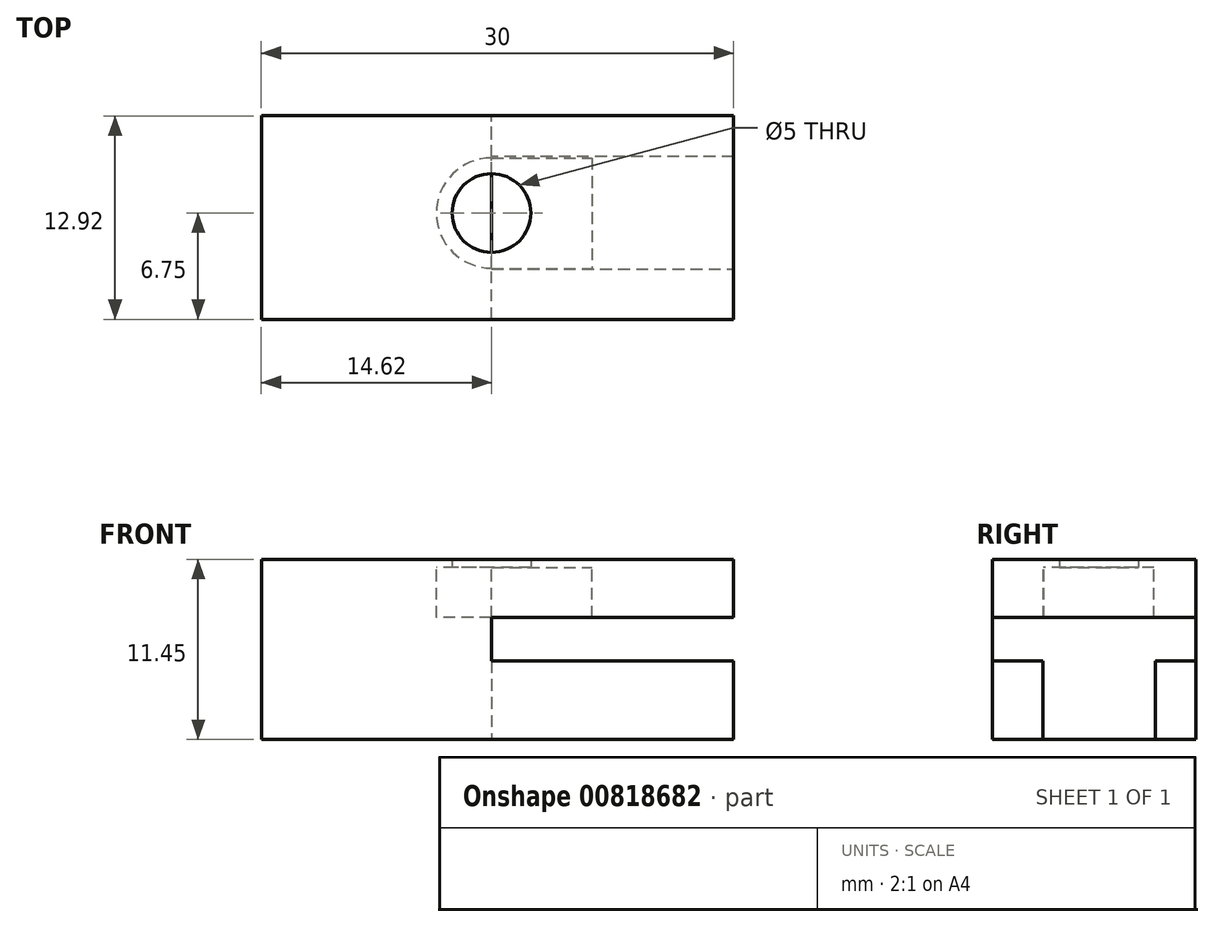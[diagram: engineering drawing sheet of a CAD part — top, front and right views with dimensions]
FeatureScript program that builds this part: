
annotation { "Feature Type Name" : "Feature", "Feature Type Description" : "" }
export const myFeature = defineFeature(function(context is Context, id is Id, definition is map)
    precondition{}
    {
        {
            var Q0;
            Q0=qCreatedBy(makeId("Top.planeOp"),FACE);
            var sketch = newSketch(context, id + "F0", { "sketchPlane" : qUnion([Q0])});
            skCircle(sketch, "E0", {"center": v(0, 0) * mm, "radius": 2.5 * mm});
            skCircle(sketch, "E1", {"center": v(0, 0) * mm, "radius": 3.5 * mm});
            skLineSegment(sketch, "E2.bottom", {"start": v(-14.62, 6.17) * mm, "end": v(15.38, 6.17) * mm});
            skLineSegment(sketch, "E2.top", {"start": v(-14.62, -6.75) * mm, "end": v(15.38, -6.75) * mm});
            skLineSegment(sketch, "E2.left", {"start": v(-14.62, 6.17) * mm, "end": v(-14.62, -6.75) * mm});
            skLineSegment(sketch, "E2.right", {"start": v(15.38, 6.17) * mm, "end": v(15.38, -6.75) * mm});
            skLineSegment(sketch, "E3.bottom", {"start": v(0, 3.5) * mm, "end": v(6.4, 3.5) * mm});
            skLineSegment(sketch, "E3.top", {"start": v(0, -3.52) * mm, "end": v(6.4, -3.52) * mm});
            skLineSegment(sketch, "E3.left", {"start": v(0, 3.5) * mm, "end": v(0, -3.52) * mm});
            skLineSegment(sketch, "E3.right", {"start": v(6.4, 3.5) * mm, "end": v(6.4, -3.52) * mm});
            skLineSegment(sketch, "E4", {"start": v(0, -6.75) * mm, "end": v(0, -3.52) * mm});
            skPoint(sketch, "E4.startSnap0", {"position": v(0.38, -6.75) * mm});
            skLineSegment(sketch, "E5", {"start": v(0, 3.5) * mm, "end": v(0, 6.17) * mm});
            skSolve(sketch);
        }
        {
            var Q0;
            {var subQ0=sQuery(id+"F0.wireOp",EDGE,"E2.right");Q0=makeQuery(id+"F0.imprint","IMPRINT",FACE,{"disambiguationData":[TD([[makeQuery(id+"F0.imprint","IMPRINT",EDGE,{"derivedFrom":subQ0}),-1.0]])]});}
            extrude(context, id + "F1", {"entities" : qUnion([Q0]), "oppositeDirection" : true, "depth" : 3.2 * mm, "offsetDistance" : 25 * mm});
        }
        {
            var Q0;
            {var subQ0=sQuery(id+"F0.wireOp",EDGE,"E2.left");Q0=makeQuery(id+"F0.imprint","IMPRINT",FACE,{"disambiguationData":[TD([[makeQuery(id+"F0.imprint","IMPRINT",EDGE,{"derivedFrom":subQ0}),1.0]])]});}
            var Q1;
            {var subQ0=sQuery(id+"F0.wireOp",EDGE,"E2.right");Q1=makeQuery(id+"F0.imprint","IMPRINT",FACE,{"disambiguationData":[TD([[makeQuery(id+"F0.imprint","IMPRINT",EDGE,{"derivedFrom":subQ0}),-1.0]])]});}
            var Q2;
            {var subQ1=sQuery(id+"F0.wireOp",EDGE,"E3.bottom");Q2=makeQuery(id+"F0.imprint","IMPRINT",FACE,{"disambiguationData":[TD([[makeQuery(id+"F0.imprint","IMPRINT",EDGE,{"derivedFrom":subQ1}),-1.0]])]});}
            var Q3;
            {var subQ0=sQuery(id+"F0.wireOp",EDGE,"agpa1uLy-kznM-YiDf-rWsz-rp6aeypRYiV5");var subQ1=sQuery(id+"F0.wireOp",EDGE,"E0");var subQ2=makeQuery(id+"F0.imprint","INTERSECT",VERTEX,{"disambiguationData":[OD(0.0)],"derivedFrom":[subQ1,subQ0]});Q3=makeQuery(id+"F0.imprint","IMPRINT",FACE,{"disambiguationData":[TD([[makeQuery(id+"F0.imprint","IMPRINT",EDGE,{"disambiguationData":[TD([[subQ2,-1.0]])],"derivedFrom":subQ1}),-1.0]])]});}
            var Q4;
            {var subQ0=sQuery(id+"F0.wireOp",EDGE,"agpa1uLy-kznM-YiDf-rWsz-rp6aeypRYiV5");var subQ1=sQuery(id+"F0.wireOp",EDGE,"E0");var subQ2=makeQuery(id+"F0.imprint","INTERSECT",VERTEX,{"disambiguationData":[OD(0.0)],"derivedFrom":[subQ1,subQ0]});Q4=makeQuery(id+"F0.imprint","IMPRINT",FACE,{"disambiguationData":[TD([[makeQuery(id+"F0.imprint","IMPRINT",EDGE,{"disambiguationData":[TD([[subQ2,1.0]])],"derivedFrom":subQ1}),-1.0]])]});}
            extrude(context, id + "F2", {"entities" : qUnion([Q0, Q1, Q2, Q3, Q4]), "operationType" : NewBodyOperationType.ADD, "depth" : .5 * mm, "offsetDistance" : 25 * mm});
        }
        {
            var Q0;
            {var subQ0=sQuery(id+"F0.wireOp",EDGE,"E2.left");Q0=makeQuery(id+"F0.imprint","IMPRINT",FACE,{"disambiguationData":[TD([[makeQuery(id+"F0.imprint","IMPRINT",EDGE,{"derivedFrom":subQ0}),1.0]])]});}
            extrude(context, id + "F3", {"entities" : qUnion([Q0]), "operationType" : NewBodyOperationType.ADD, "oppositeDirection" : true, "depth" : 3.2 * mm, "offsetDistance" : 25 * mm});
        }
        {
            var Q0;
            Q0=makeQuery(id+"F3.opExtrude","CAP_FACE",FACE,{"disambiguationData":[OSD([sQuery(id+"F0.wireOp",EDGE,"E1"),sQuery(id+"F0.wireOp",EDGE,"E2.bottom"),sQuery(id+"F0.wireOp",EDGE,"E2.top"),sQuery(id+"F0.wireOp",EDGE,"E2.left"),sQuery(id+"F0.wireOp",EDGE,"E3.left"),sQuery(id+"F0.wireOp",EDGE,"E4"),sQuery(id+"F0.wireOp",EDGE,"E5")])],"isStart":false});
            var sketch = newSketch(context, id + "F4", { "sketchPlane" : qUnion([Q0])});
            skLineSegment(sketch, "E6.bottom", {"start": v(-14.62, 6.75) * mm, "end": v(0, 6.75) * mm});
            skLineSegment(sketch, "E6.top", {"start": v(-14.62, -6.17) * mm, "end": v(0, -6.17) * mm});
            skLineSegment(sketch, "E6.left", {"start": v(-14.62, 6.75) * mm, "end": v(-14.62, -6.17) * mm});
            skLineSegment(sketch, "E6.right", {"start": v(0, 6.75) * mm, "end": v(0, -6.17) * mm});
            skSolve(sketch);
        }
        {
            var Q0;
            {var subQ1=sQuery(id+"F4.wireOp",EDGE,"E6.bottom");Q0=makeQuery(id+"F4.imprint","IMPRINT",FACE,{"disambiguationData":[TD([[makeQuery(id+"F4.imprint","IMPRINT",EDGE,{"derivedFrom":subQ1}),-1.0]])]});}
            var Q1;
            {var subQ1=makeQuery(id+"F3.opExtrude","CAP_EDGE",EDGE,{"disambiguationData":[OSD([sQuery(id+"F0.wireOp",EDGE,"E1")])],"isStart":false});Q1=makeQuery(id+"F4.imprint","IMPRINT",FACE,{"disambiguationData":[TD([[makeQuery(id+"F4.imprint","IMPRINT",EDGE,{"derivedFrom":subQ1}),-1.0]])]});}
            extrude(context, id + "F5", {"entities" : qUnion([Q0, Q1]), "operationType" : NewBodyOperationType.ADD, "depth" : 2.75 * mm, "offsetDistance" : 25 * mm});
        }
        {
            var Q0;
            Q0=makeQuery(id+"F5.opExtrude","CAP_FACE",FACE,{"disambiguationData":[OSD([sQuery(id+"F4.wireOp",EDGE,"E6.bottom"),sQuery(id+"F4.wireOp",EDGE,"E6.top"),sQuery(id+"F4.wireOp",EDGE,"E6.left"),sQuery(id+"F4.wireOp",EDGE,"E6.right")])],"isStart":false});
            extrude(context, id + "F6", {"entities" : qUnion([Q0]), "depth" : 5 * mm, "offsetDistance" : 25 * mm});
        }
        {
            var Q0;
            Q0=makeQuery(id+"F6.opExtrude","CAP_FACE",FACE,{"disambiguationData":[OSD([sQuery(id+"F4.wireOp",EDGE,"E6.bottom"),sQuery(id+"F4.wireOp",EDGE,"E6.top"),sQuery(id+"F4.wireOp",EDGE,"E6.left"),sQuery(id+"F4.wireOp",EDGE,"E6.right")])],"isStart":false});
            var sketch = newSketch(context, id + "F7", { "sketchPlane" : qUnion([Q0])});
            skLineSegment(sketch, "E7.bottom", {"start": v(0, 6.75) * mm, "end": v(15.37, 6.75) * mm});
            skLineSegment(sketch, "E7.top", {"start": v(0, 3.57) * mm, "end": v(15.37, 3.57) * mm});
            skLineSegment(sketch, "E7.left", {"start": v(0, 6.75) * mm, "end": v(0, 3.57) * mm});
            skLineSegment(sketch, "E7.right", {"start": v(15.37, 6.75) * mm, "end": v(15.37, 3.57) * mm});
            skLineSegment(sketch, "E8.bottom", {"start": v(15.37, 3.57) * mm, "end": v(6.37, 3.57) * mm});
            skLineSegment(sketch, "E8.top", {"start": v(15.37, -3.58) * mm, "end": v(6.37, -3.58) * mm});
            skLineSegment(sketch, "E8.left", {"start": v(15.37, 3.57) * mm, "end": v(15.37, -3.58) * mm});
            skLineSegment(sketch, "E8.right", {"start": v(6.37, 3.57) * mm, "end": v(6.37, -3.58) * mm});
            skLineSegment(sketch, "E9.bottom", {"start": v(15.37, -6.17) * mm, "end": v(0, -6.17) * mm});
            skLineSegment(sketch, "E9.top", {"start": v(15.37, -3.58) * mm, "end": v(0, -3.58) * mm});
            skLineSegment(sketch, "E9.left", {"start": v(15.37, -6.17) * mm, "end": v(15.37, -3.58) * mm});
            skLineSegment(sketch, "E9.right", {"start": v(0, -6.17) * mm, "end": v(0, -3.58) * mm});
            skSolve(sketch);
        }
        {
            var Q0;
            Q0=makeQuery(id+"F7.imprint","IMPRINT",FACE,{"disambiguationData":[TD([[makeQuery(id+"F7.imprint","IMPRINT",EDGE,{"derivedFrom":sQuery(id+"F7.wireOp",EDGE,"E7.bottom")}),-1.0]])]});
            var Q1;
            Q1=makeQuery(id+"F7.imprint","IMPRINT",FACE,{"disambiguationData":[TD([[makeQuery(id+"F7.imprint","IMPRINT",EDGE,{"derivedFrom":sQuery(id+"F7.wireOp",EDGE,"E8.bottom")}),1.0]])]});
            var Q2;
            Q2=makeQuery(id+"F7.imprint","IMPRINT",FACE,{"disambiguationData":[TD([[makeQuery(id+"F7.imprint","IMPRINT",EDGE,{"derivedFrom":sQuery(id+"F7.wireOp",EDGE,"E9.bottom")}),-1.0]])]});
            extrude(context, id + "F8", {"entities" : qUnion([Q0, Q1, Q2]), "operationType" : NewBodyOperationType.ADD, "oppositeDirection" : true, "depth" : 5 * mm, "offsetDistance" : 25 * mm});
        }
    });
